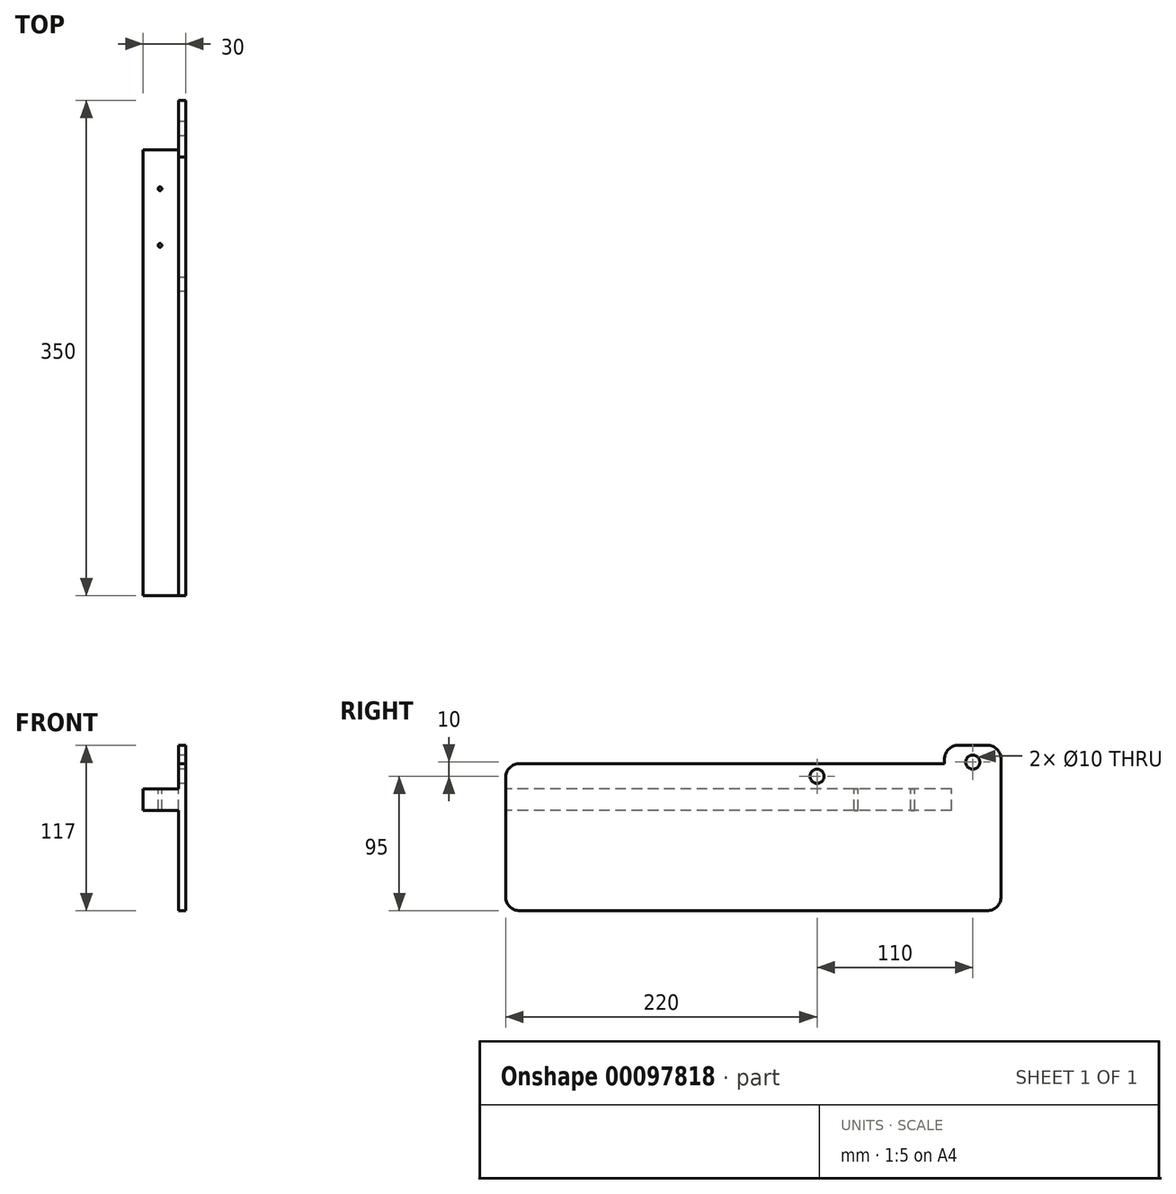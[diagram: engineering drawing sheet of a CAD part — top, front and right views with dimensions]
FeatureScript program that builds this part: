
annotation { "Feature Type Name" : "Feature", "Feature Type Description" : "" }
export const myFeature = defineFeature(function(context is Context, id is Id, definition is map)
    precondition{}
    {
        {
            var Q0;
            Q0=qCreatedBy(makeId("Right.planeOp"),FACE);
            var sketch = newSketch(context, id + "F0", { "sketchPlane" : qUnion([Q0])});
            skLineSegment(sketch, "E0", {"start": v(-320, -1) * mm, "end": v(-20, -1) * mm});
            skLineSegment(sketch, "E1", {"start": v(-20, -1) * mm, "end": v(-20, 2) * mm});
            skLineSegment(sketch, "E2", {"start": v(-10, 12) * mm, "end": v(10, 12) * mm});
            skLineSegment(sketch, "E3", {"start": v(20, 2) * mm, "end": v(20, -95) * mm});
            skLineSegment(sketch, "E4", {"start": v(10, -105) * mm, "end": v(-320, -105) * mm});
            skLineSegment(sketch, "E5", {"start": v(-330, -95) * mm, "end": v(-330, -11) * mm});
            skCircle(sketch, "E6", {"center": v(0, 0) * mm, "radius": 5 * mm});
            skCircle(sketch, "E7", {"center": v(-110, -10) * mm, "radius": 5 * mm});
            skPoint(sketch, "E8.visualSharp", {"position": v(20, -105) * mm});
            skArc(sketch, "E8.filletArc", {"start": v(10, -105) * mm, "mid": v(17.07, -102.07) * mm, "end": v(20, -95) * mm});
            skPoint(sketch, "E9.visualSharp", {"position": v(-330, -105) * mm});
            skArc(sketch, "E9.filletArc", {"start": v(-330, -95) * mm, "mid": v(-327.07, -102.07) * mm, "end": v(-320, -105) * mm});
            skPoint(sketch, "E10.visualSharp", {"position": v(-330, -1) * mm});
            skArc(sketch, "E10.filletArc", {"start": v(-320, -1) * mm, "mid": v(-327.07, -3.93) * mm, "end": v(-330, -11) * mm});
            skPoint(sketch, "E11.visualSharp", {"position": v(-20, 12) * mm});
            skArc(sketch, "E11.filletArc", {"start": v(-10, 12) * mm, "mid": v(-17.07, 9.07) * mm, "end": v(-20, 2) * mm});
            skPoint(sketch, "E12.visualSharp", {"position": v(20, 12) * mm});
            skArc(sketch, "E12.filletArc", {"start": v(20, 2) * mm, "mid": v(17.07, 9.07) * mm, "end": v(10, 12) * mm});
            skSolve(sketch);
        }
        {
            var Q0;
            Q0=makeQuery(id+"F0.imprint","IMPRINT",FACE,{"disambiguationData":[TD([[makeQuery(id+"F0.imprint","IMPRINT",EDGE,{"derivedFrom":sQuery(id+"F0.wireOp",EDGE,"E0")}),-1.0]])]});
            var Q1;
            Q1=qSketchRegion(id+"F0",true);
            extrude(context, id + "F1", {"entities" : qUnion([Q0, Q1]), "depth" : 5 * mm});
        }
        {
            var Q0;
            Q0=makeQuery(id+"F1.opExtrude","CAP_FACE",FACE,{"disambiguationData":[OSD([sQuery(id+"F0.wireOp",EDGE,"E0"),sQuery(id+"F0.wireOp",EDGE,"E1"),sQuery(id+"F0.wireOp",EDGE,"E2"),sQuery(id+"F0.wireOp",EDGE,"E3"),sQuery(id+"F0.wireOp",EDGE,"E4"),sQuery(id+"F0.wireOp",EDGE,"E5"),sQuery(id+"F0.wireOp",EDGE,"E6"),sQuery(id+"F0.wireOp",EDGE,"E7"),sQuery(id+"F0.wireOp",EDGE,"E8.filletArc"),sQuery(id+"F0.wireOp",EDGE,"E9.filletArc"),sQuery(id+"F0.wireOp",EDGE,"E10.filletArc"),sQuery(id+"F0.wireOp",EDGE,"E11.filletArc"),sQuery(id+"F0.wireOp",EDGE,"E12.filletArc")])],"isStart":true});
            var sketch = newSketch(context, id + "F2", { "sketchPlane" : qUnion([Q0])});
            skLineSegment(sketch, "E13.bottom", {"start": v(15, -34) * mm, "end": v(330, -34) * mm});
            skLineSegment(sketch, "E13.top", {"start": v(15, -19) * mm, "end": v(330, -19) * mm});
            skLineSegment(sketch, "E13.left", {"start": v(15, -34) * mm, "end": v(15, -19) * mm});
            skLineSegment(sketch, "E13.right", {"start": v(330, -34) * mm, "end": v(330, -19) * mm});
            skSolve(sketch);
        }
        {
            var Q0;
            Q0 = qSketchRegion(id + "F2", true);
            extrude(context, id + "F3", {"entities" : qUnion([Q0]), "operationType" : NewBodyOperationType.ADD, "depth" : 25 * mm});
        }
        {
            var Q0;
            Q0=makeQuery(id+"F3.opExtrude","SWEPT_FACE",FACE,{"disambiguationData":[OSD([sQuery(id+"F2.wireOp",EDGE,"E13.top")])]});
            var sketch = newSketch(context, id + "F4", { "sketchPlane" : qUnion([Q0])});
            skCircle(sketch, "E14", {"center": v(-13, -42.4) * mm, "radius": 3.64 * mm});
            skCircle(sketch, "E15", {"center": v(-13, -82.4) * mm, "radius": 3.2 * mm});
            skLineSegment(sketch, "E16", {"start": v(-13, -82.4) * mm, "end": v(-13, -27.13) * mm, "construction": true});
            skSolve(sketch);
        }
        {
            var Q0;
            Q0=sQuery(id+"F4.wireOp",VERTEX,"E14.center");
            var Q1;
            Q1=sQuery(id+"F4.wireOp",VERTEX,"E15.center");
            var Q2;
            Q2=makeQuery(id+"F1.opExtrude","SWEPT_BODY",BODY,{"disambiguationData":[OSD([sQuery(id+"F0.wireOp",EDGE,"E0"),sQuery(id+"F0.wireOp",EDGE,"E1"),sQuery(id+"F0.wireOp",EDGE,"E2"),sQuery(id+"F0.wireOp",EDGE,"E3"),sQuery(id+"F0.wireOp",EDGE,"E4"),sQuery(id+"F0.wireOp",EDGE,"E5"),sQuery(id+"F0.wireOp",EDGE,"E6"),sQuery(id+"F0.wireOp",EDGE,"E7"),sQuery(id+"F0.wireOp",EDGE,"E8.filletArc"),sQuery(id+"F0.wireOp",EDGE,"E9.filletArc"),sQuery(id+"F0.wireOp",EDGE,"E10.filletArc"),sQuery(id+"F0.wireOp",EDGE,"E11.filletArc"),sQuery(id+"F0.wireOp",EDGE,"E12.filletArc")])]});
            hole(context, id + "F5", {"style" : HoleStyle.SIMPLE, "endStyle" : HoleEndStyle.THROUGH, "holeDiameter" : 2.6 * mm, "locations" : qUnion([Q0, Q1]), "scope" : qUnion([Q2]), "isTappedThrough" : true});
        }
    });
